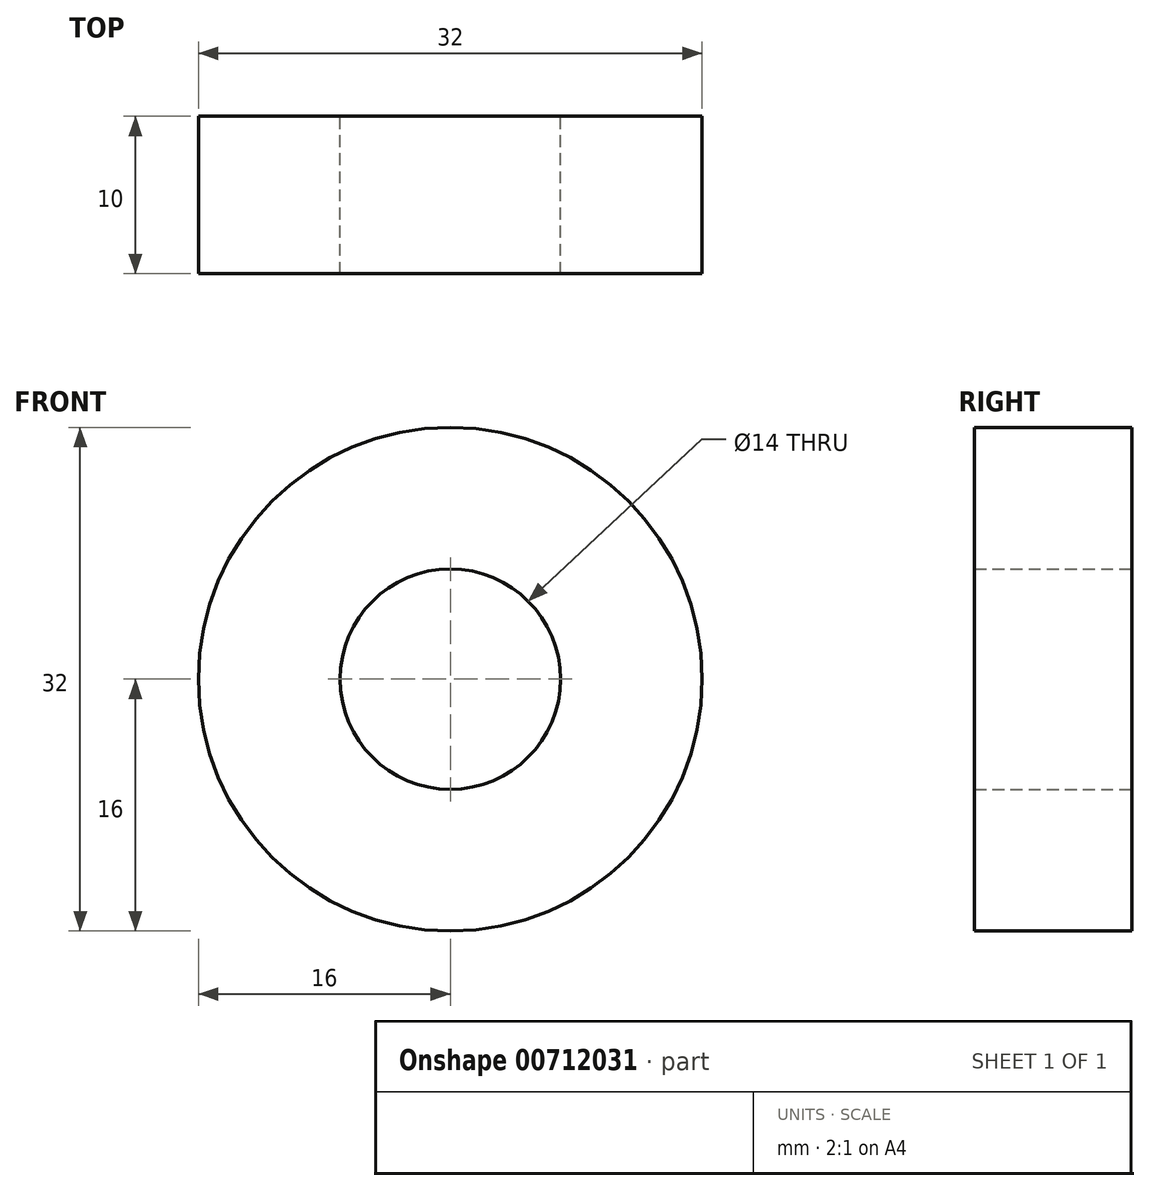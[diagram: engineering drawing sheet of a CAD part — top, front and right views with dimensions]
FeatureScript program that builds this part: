
annotation { "Feature Type Name" : "Feature", "Feature Type Description" : "" }
export const myFeature = defineFeature(function(context is Context, id is Id, definition is map)
    precondition{}
    {
        {
            var Q0;
            Q0=qCreatedBy(makeId("Front.planeOp"),FACE);
            var sketch = newSketch(context, id + "F0", { "sketchPlane" : qUnion([Q0])});
            skCircle(sketch, "E0", {"center": v(0, 0) * mm, "radius": 16 * mm});
            skCircle(sketch, "E1", {"center": v(0, 0) * mm, "radius": 7 * mm});
            skSolve(sketch);
        }
        {
            var Q0;
            Q0=makeQuery(id+"F0.imprint","IMPRINT",FACE,{"disambiguationData":[TD([[makeQuery(id+"F0.imprint","IMPRINT",EDGE,{"derivedFrom":sQuery(id+"F0.wireOp",EDGE,"E0")}),1.0]])]});
            extrude(context, id + "F1", {"entities" : qUnion([Q0]), "depth" : 10 * mm, "offsetDistance" : 25 * mm});
        }
    });
